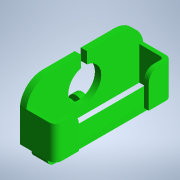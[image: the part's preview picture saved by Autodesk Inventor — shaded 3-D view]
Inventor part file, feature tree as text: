
AUTODESK INVENTOR PART (.ipt)
format: ipt  version: 2022 (Build 260153000, 153)  size: 269,312 bytes
history: native  units: mm
features: extrude x11, sketch x11, reference x7, other x5, fillet x4, projected_geometry x4
ambient origin geometry x8: Origin, YZ Plane, XZ Plane, XY Plane, X Axis, Y Axis, Z Axis, Center Point
bodies: Body1 (feature_tree)
feature tree (42):
  other  "Твердое тело1"
  extrude  "Выдавливание1"  Depth=4.0mm TaperAngle=0.0deg
  extrude  "Выдавливание2"  Depth=4.0mm
  extrude  "Выдавливание3"  Depth=4.5mm
  extrude  "Выдавливание4"  Depth=3.0mm TaperAngle=0.0deg
  extrude  "Выдавливание5"  Depth=4.0mm TaperAngle=0.0deg
  extrude  "Выдавливание6"  Depth=3.0mm
  extrude  "Выдавливание7"  Depth=3.0mm
  extrude  "Выдавливание8"  Depth=4.0mm TaperAngle=0.0deg
  fillet  "Сопряжение1"  Radius=4.0mm
  extrude  "Выдавливание9"  Depth=2.5mm
  fillet  "Сопряжение2"  Radius=2.5mm
  fillet  "Сопряжение3"  Radius=15.5mm
  fillet  "Сопряжение4"  Radius=15.5mm
  extrude  "Выдавливание10"  Depth=4.0mm TaperAngle=0.0deg
  extrude  "Выдавливание11"  Depth=4.0mm
  sketch  "Эскиз1"
  reference  "Ссылка1"
  sketch  "Эскиз2"
  projected_geometry  "Спроецированная петля1"
  sketch  "Эскиз3"
  projected_geometry  "Спроецированная петля2"
  sketch  "Эскиз4"
  reference  "Ссылка2"
  reference  "Ссылка3"
  reference  "Ссылка4"
  reference  "Ссылка5"
  reference  "Ссылка6"
  sketch  "Эскиз5"
  reference  "Ссылка7"
  sketch  "Эскиз6"
  projected_geometry  "Спроецированная петля3"
  sketch  "Эскиз7"
  sketch  "Эскиз8"
  sketch  "Эскиз9"
  sketch  "Эскиз10"
  sketch  "Эскиз11"
  projected_geometry  "Спроецированная петля4"
  other  "<path> - Robot.iam"
  other  "000.000 - Robot.iam"
  other  "camera_holder:1"
  other  "C525:1"
note: 1 file-system path scrubbed to <path> (originals preserved in map.json)
